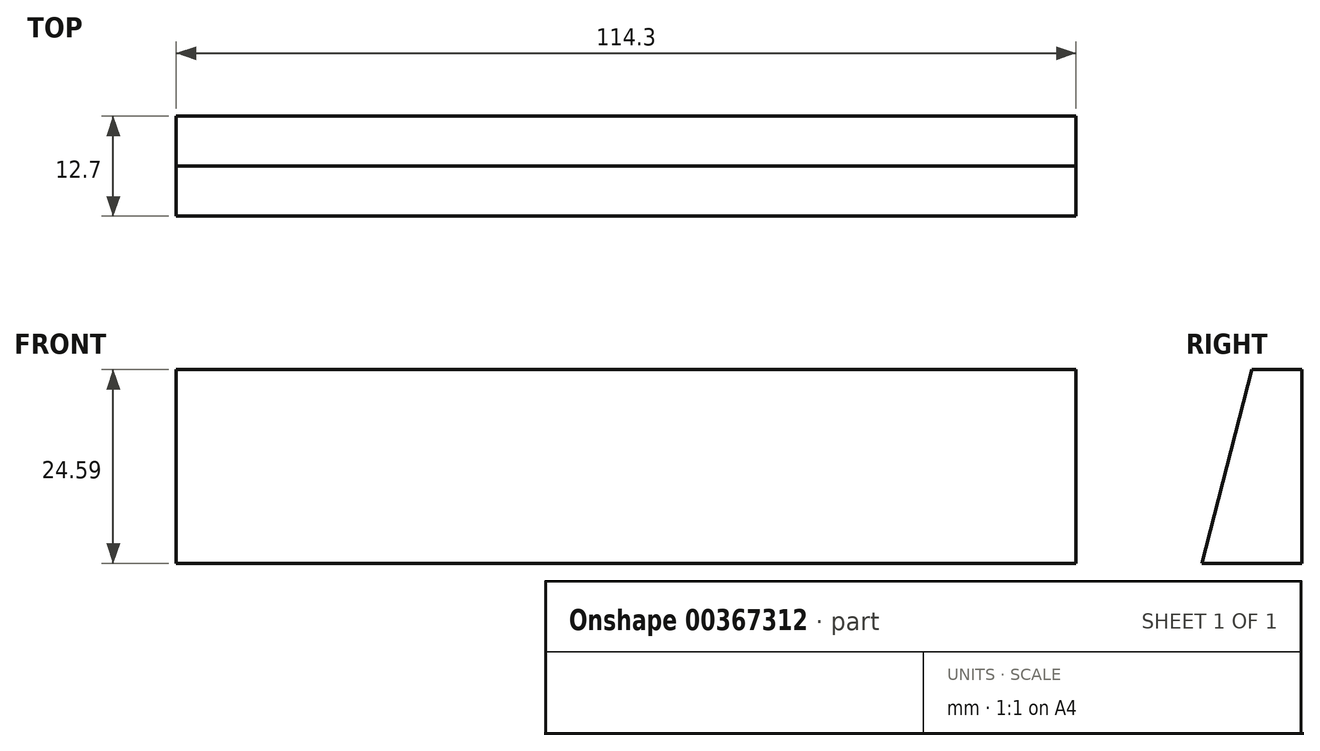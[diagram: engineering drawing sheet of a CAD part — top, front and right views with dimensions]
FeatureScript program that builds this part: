
annotation { "Feature Type Name" : "Feature", "Feature Type Description" : "" }
export const myFeature = defineFeature(function(context is Context, id is Id, definition is map)
    precondition{}
    {
        {
            var Q0;
            Q0=qCreatedBy(makeId("Right.planeOp"),FACE);
            var sketch = newSketch(context, id + "F0", { "sketchPlane" : qUnion([Q0])});
            skLineSegment(sketch, "E0", {"start": v(0, 24.6) * mm, "end": v(-6.35, 24.6) * mm});
            skLineSegment(sketch, "E1", {"start": v(-6.35, 24.6) * mm, "end": v(-12.7, 0) * mm});
            skLineSegment(sketch, "E2", {"start": v(-12.7, 0) * mm, "end": v(0, 0) * mm});
            skLineSegment(sketch, "E3", {"start": v(0, 24.6) * mm, "end": v(0, 0) * mm});
            skSolve(sketch);
        }
        {
            var Q0;
            Q0=makeQuery(id+"F0.imprint","IMPRINT",FACE,{"disambiguationData":[TD([[makeQuery(id+"F0.imprint","IMPRINT",EDGE,{"derivedFrom":sQuery(id+"F0.wireOp",EDGE,"E0")}),1.0]])]});
            extrude(context, id + "F1", {"entities" : qUnion([Q0]), "depth" : 114.3 * mm});
        }
    });
